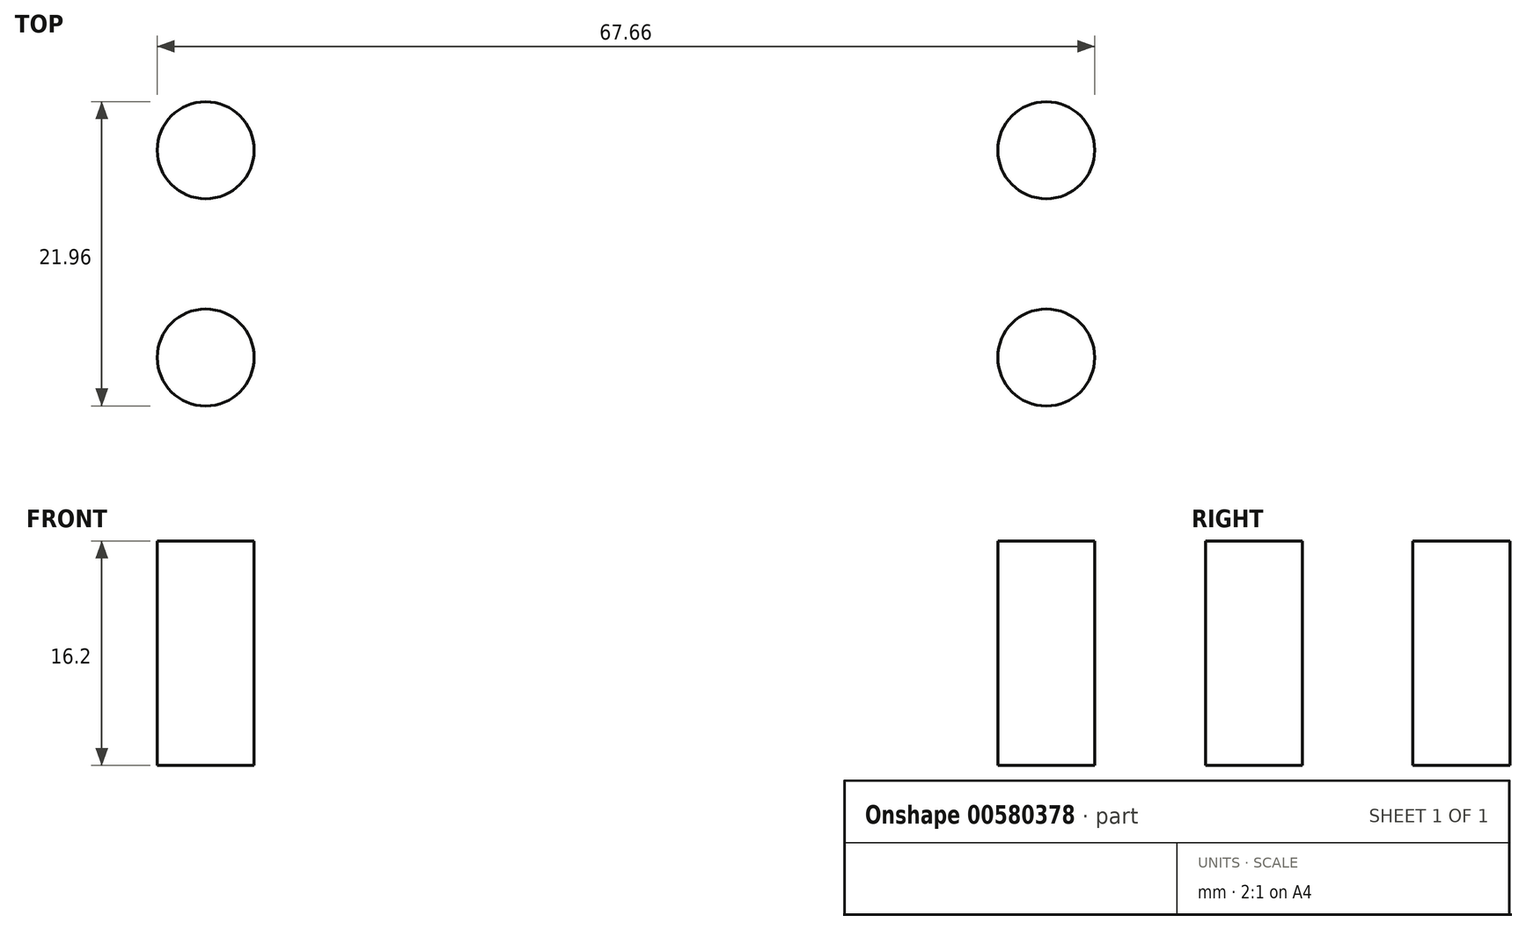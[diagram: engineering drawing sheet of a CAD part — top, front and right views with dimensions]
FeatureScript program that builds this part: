
annotation { "Feature Type Name" : "Feature", "Feature Type Description" : "" }
export const myFeature = defineFeature(function(context is Context, id is Id, definition is map)
    precondition{}
    {
        {
            var Q0;
            Q0=qCreatedBy(makeId("Top.planeOp"),FACE);
            var sketch = newSketch(context, id + "F0", { "sketchPlane" : qUnion([Q0])});
            skCircle(sketch, "E0", {"center": v(-45.73, 10.2) * mm, "radius": 3.5 * mm});
            skCircle(sketch, "E1", {"center": v(-45.73, -4.76) * mm, "radius": 3.5 * mm});
            skCircle(sketch, "E2", {"center": v(14.93, 10.2) * mm, "radius": 3.5 * mm});
            skCircle(sketch, "E3", {"center": v(14.93, -4.76) * mm, "radius": 3.5 * mm});
            skSolve(sketch);
        }
        {
            var Q0;
            Q0=makeQuery(id+"F0.imprint","IMPRINT",FACE,{"disambiguationData":[TD([[makeQuery(id+"F0.imprint","IMPRINT",EDGE,{"derivedFrom":sQuery(id+"F0.wireOp",EDGE,"E0")}),1.0]])]});
            var Q1;
            Q1=makeQuery(id+"F0.imprint","IMPRINT",FACE,{"disambiguationData":[TD([[makeQuery(id+"F0.imprint","IMPRINT",EDGE,{"derivedFrom":sQuery(id+"F0.wireOp",EDGE,"E2")}),1.0]])]});
            var Q2;
            Q2=makeQuery(id+"F0.imprint","IMPRINT",FACE,{"disambiguationData":[TD([[makeQuery(id+"F0.imprint","IMPRINT",EDGE,{"derivedFrom":sQuery(id+"F0.wireOp",EDGE,"E3")}),1.0]])]});
            var Q3;
            Q3=makeQuery(id+"F0.imprint","IMPRINT",FACE,{"disambiguationData":[TD([[makeQuery(id+"F0.imprint","IMPRINT",EDGE,{"derivedFrom":sQuery(id+"F0.wireOp",EDGE,"E1")}),1.0]])]});
            extrude(context, id + "F1", {"entities" : qUnion([Q0, Q1, Q2, Q3]), "depth" : 16.2 * mm, "offsetDistance" : 25 * mm});
        }
    });
